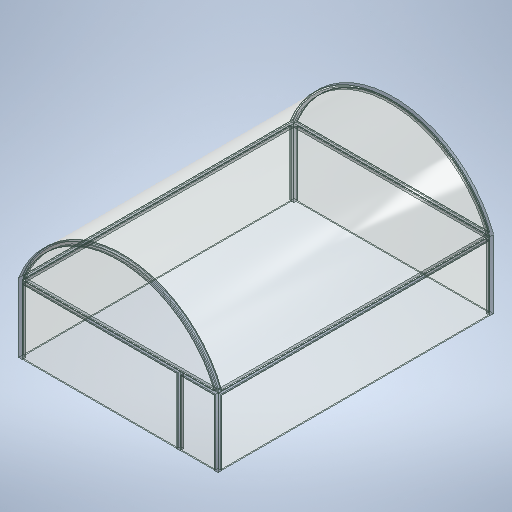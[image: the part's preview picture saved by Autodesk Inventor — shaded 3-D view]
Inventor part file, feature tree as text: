
AUTODESK INVENTOR PART (.ipt)
format: ipt  version: 2025.3 (Build 293356000, 356)  size: 485,376 bytes
history: native  units: mm
features: extrude x12, sketch x12, other x1, shell x1
ambient origin geometry x8: Origin, YZ Plane, XZ Plane, XY Plane, X Axis, Y Axis, Z Axis, Center Point
bodies: Body1 (feature_tree)
feature tree (26):
  other  "Sólido1"
  extrude  "Extrusión1"  Depth=5800.0mm
  extrude  "Extrusión2"  Depth=3102.5mm
  shell  "Vaciado1"  Thickness=0.0mm
  extrude  "Extrusión3"  Depth=100.0mm
  extrude  "Extrusión4"  Depth=100.0mm
  extrude  "Extrusión5"  Depth=100.0mm
  extrude  "Extrusión6"  Depth=100.0mm
  extrude  "Extrusión7"  Depth=2000.0mm TaperAngle=0.0deg
  extrude  "Extrusión8"  Depth=10.0mm
  extrude  "Extrusión12"  Depth=10.0mm
  extrude  "Extrusión14"  Depth=10.0mm
  extrude  "Extrusión15"  Depth=10.0mm
  extrude  "Extrusión16"  Depth=10.0mm TaperAngle=0.0deg
  sketch  "Boceto1"  dims[d0=8000.0mm d1=5800.0mm]
  sketch  "Boceto2"  dims[d2=4000.0mm d3=0.0mm d6=3102.5mm d7=0.0mm d8=0.0mm]
  sketch  "Boceto4"  dims[d9=30.0mm d16=100.0mm]
  sketch  "Boceto7"  dims[d17=100.0mm d18=100.0mm]
  sketch  "Boceto8"  dims[d19=100.0mm d20=100.0mm]
  sketch  "Boceto9"  dims[d21=100.0mm d22=100.0mm]
  sketch  "Boceto10"  dims[d23=100.0mm d24=2000.0mm d25=0.0mm]
  sketch  "Boceto11"  dims[d26=10.0mm d27=10.0mm]
  sketch  "Boceto15"  dims[d28=10.0mm d29=10.0mm]
  sketch  "Boceto17"  dims[d30=10.0mm d31=10.0mm]
  sketch  "Boceto18"  dims[d32=10.0mm d33=10.0mm]
  sketch  "Boceto19"  dims[d34=3112.0mm d35=10.0mm d36=100.0mm d37=0.0mm d38=0.0mm d39=100.0mm d40=5800.0mm d41=0.0mm d42=10.0mm d43=0.0mm d44=100.0mm d45=100.0mm d46=7900.0mm d47=0.0mm d48=5800.0mm d49=0.0mm d56=110.0mm d57=0.0mm d60=110.0mm d61=0.0mm d62=70.0mm d63=0.0mm d64=100.0mm d65=1000.0mm d66=10.0mm d67=100.0mm d68=0.0mm d69=0.0mm]
